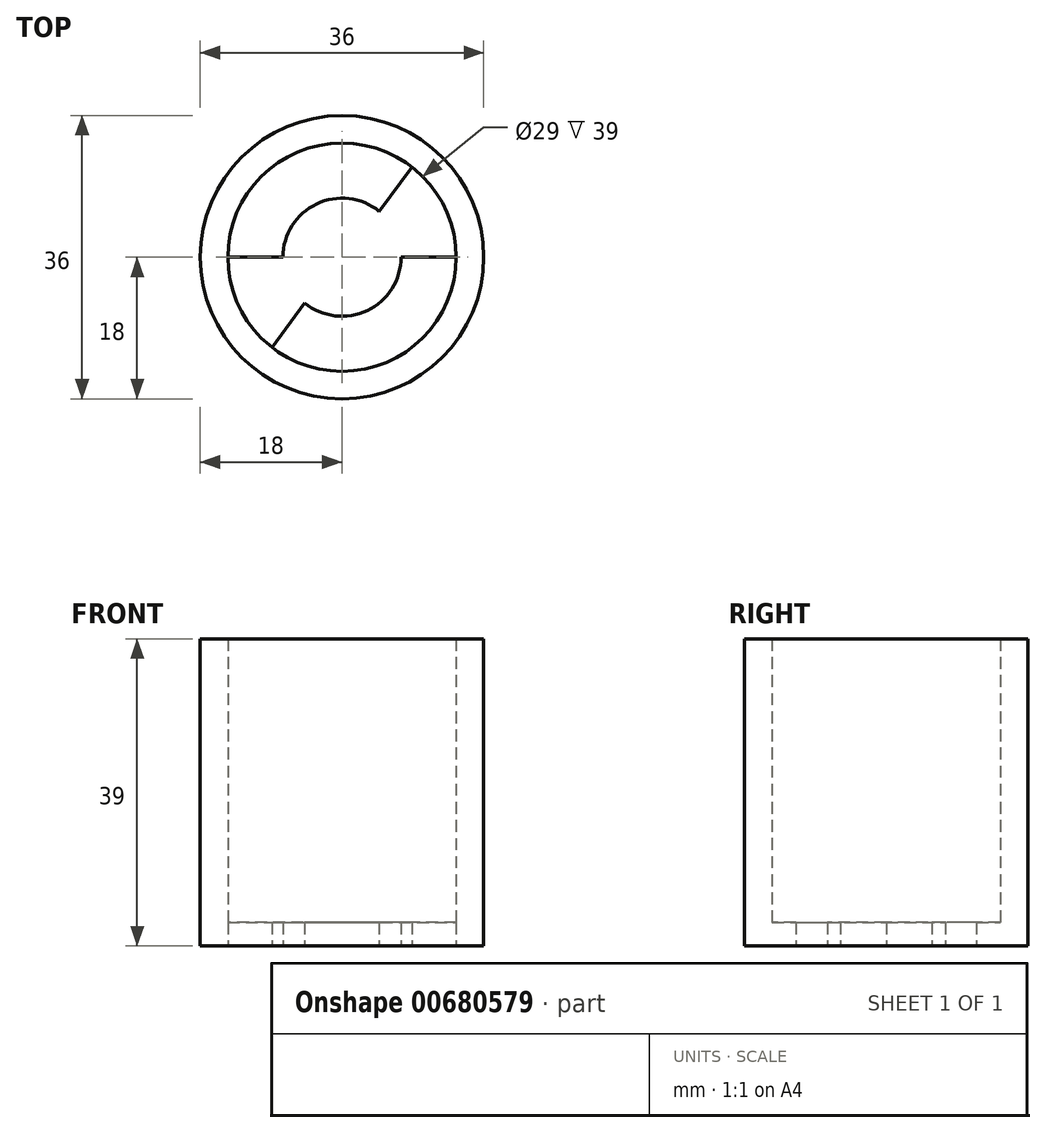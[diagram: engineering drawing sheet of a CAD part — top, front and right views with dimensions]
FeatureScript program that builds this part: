
annotation { "Feature Type Name" : "Feature", "Feature Type Description" : "" }
export const myFeature = defineFeature(function(context is Context, id is Id, definition is map)
    precondition{}
    {
        {
            var Q0;
            Q0=qCreatedBy(makeId("Top.planeOp"),FACE);
            var sketch = newSketch(context, id + "F0", { "sketchPlane" : qUnion([Q0])});
            skCircle(sketch, "E0", {"center": v(0, 0) * mm, "radius": 14.5 * mm});
            skCircle(sketch, "E1", {"center": v(0, 0) * mm, "radius": 18 * mm});
            skSolve(sketch);
        }
        {
            var Q0;
            Q0 = qSketchRegion(id + "F0", true);
            extrude(context, id + "F1", {"entities" : qUnion([Q0]), "depth" : 36 * mm, "offsetDistance" : 25 * mm});
        }
        {
            var Q0;
            Q0=makeQuery(id+"F1.opExtrude","CAP_FACE",FACE,{"disambiguationData":[OSD([sQuery(id+"F0.wireOp",EDGE,"E0"),sQuery(id+"F0.wireOp",EDGE,"E1")])],"isStart":true});
            var sketch = newSketch(context, id + "F2", { "sketchPlane" : qUnion([Q0])});
            skCircle(sketch, "E2.0", {"center": v(0, 0) * mm, "radius": 18 * mm});
            skSolve(sketch);
        }
        {
            var Q0;
            Q0 = qSketchRegion(id + "F2", true);
            extrude(context, id + "F3", {"entities" : qUnion([Q0]), "operationType" : NewBodyOperationType.ADD, "depth" : 3 * mm, "offsetDistance" : 25 * mm});
        }
        {
            var Q0;
            Q0=makeQuery(id+"F3.opExtrude","CAP_FACE",FACE,{"disambiguationData":[OSD([sQuery(id+"F2.wireOp",EDGE,"E2.0")])],"isStart":false});
            var sketch = newSketch(context, id + "F4", { "sketchPlane" : qUnion([Q0])});
            skArc(sketch, "E3.0", {"start": v(-8.87, 11.47) * mm, "mid": v(-13.02, 6.39) * mm, "end": v(-14.5, 0) * mm});
            skCircle(sketch, "E4", {"center": v(0, 0) * mm, "radius": 7.5 * mm});
            skLineSegment(sketch, "E5", {"start": v(-14.5, 0) * mm, "end": v(-7.5, 0) * mm});
            skLineSegment(sketch, "E6", {"start": v(-8.87, 11.47) * mm, "end": v(-4.73, 5.82) * mm});
            skLineSegment(sketch, "E7.1.0", {"start": v(8.87, -11.47) * mm, "end": v(4.73, -5.82) * mm});
            skLineSegment(sketch, "E7.1.1", {"start": v(14.5, 0) * mm, "end": v(7.5, 0) * mm});
            skArc(sketch, "E8.trimOffspring", {"start": v(8.87, -11.47) * mm, "mid": v(13.02, -6.39) * mm, "end": v(14.5, 0) * mm});
            skSolve(sketch);
        }
        {
            var Q0;
            Q0 = qSketchRegion(id + "F4", true);
            extrude(context, id + "F5", {"entities" : qUnion([Q0]), "operationType" : NewBodyOperationType.REMOVE, "oppositeDirection" : true, "depth" : 25 * mm, "offsetDistance" : 25 * mm});
        }
    });
